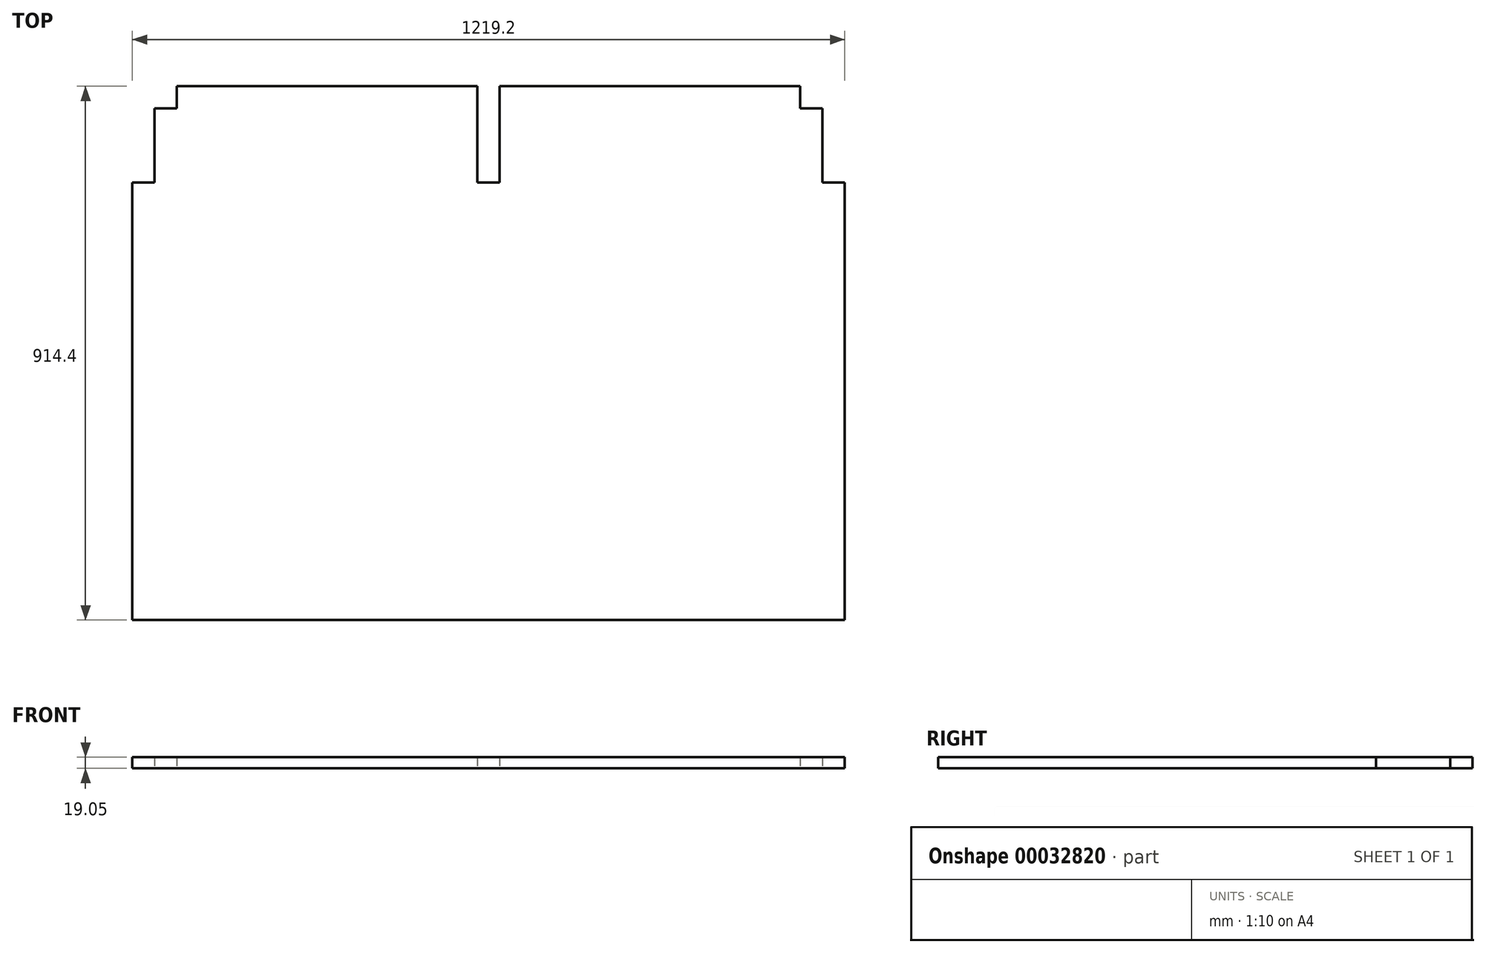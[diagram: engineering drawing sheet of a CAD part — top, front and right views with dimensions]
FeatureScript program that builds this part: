
annotation { "Feature Type Name" : "Feature", "Feature Type Description" : "" }
export const myFeature = defineFeature(function(context is Context, id is Id, definition is map)
    precondition{}
    {
        {
            var Q0;
            Q0=qCreatedBy(makeId("Top.planeOp"),FACE);
            var sketch = newSketch(context, id + "F0", { "sketchPlane" : qUnion([Q0])});
            skLineSegment(sketch, "E0.rect.bottom", {"start": v(-533.4, 539.75) * mm, "end": v(-19.05, 539.75) * mm});
            skLineSegment(sketch, "E0.rect.top", {"start": v(-609.6, -374.65) * mm, "end": v(609.6, -374.65) * mm});
            skLineSegment(sketch, "E0.rect.left", {"start": v(-609.6, 374.65) * mm, "end": v(-609.6, -374.65) * mm});
            skLineSegment(sketch, "E0.rect.right", {"start": v(609.6, 374.65) * mm, "end": v(609.6, -374.65) * mm});
            skPoint(sketch, "E0.rect.middle", {"position": v(0, 0) * mm});
            skLineSegment(sketch, "E1", {"start": v(-609.6, 374.65) * mm, "end": v(-571.5, 374.65) * mm});
            skLineSegment(sketch, "E2", {"start": v(-571.5, 374.65) * mm, "end": v(-571.5, 501.65) * mm});
            skLineSegment(sketch, "E3", {"start": v(-19.05, 539.75) * mm, "end": v(-19.05, 374.65) * mm});
            skLineSegment(sketch, "E4", {"start": v(-19.05, 374.65) * mm, "end": v(19.05, 374.65) * mm});
            skLineSegment(sketch, "E5", {"start": v(19.05, 374.65) * mm, "end": v(19.05, 539.75) * mm});
            skLineSegment(sketch, "E6", {"start": v(571.5, 501.65) * mm, "end": v(571.5, 374.65) * mm});
            skLineSegment(sketch, "E7", {"start": v(571.5, 374.65) * mm, "end": v(609.6, 374.65) * mm});
            skLineSegment(sketch, "E8", {"start": v(0, 374.65) * mm, "end": v(0, 0) * mm, "construction": true});
            skLineSegment(sketch, "E9.trimOffspring", {"start": v(19.05, 539.75) * mm, "end": v(533.4, 539.75) * mm});
            skLineSegment(sketch, "E10", {"start": v(0, -374.65) * mm, "end": v(0, 0) * mm, "construction": true});
            skLineSegment(sketch, "E11", {"start": v(609.6, 0) * mm, "end": v(0, 0) * mm, "construction": true});
            skLineSegment(sketch, "E12", {"start": v(-609.6, 0) * mm, "end": v(0, 0) * mm, "construction": true});
            skLineSegment(sketch, "E13", {"start": v(-571.5, 501.65) * mm, "end": v(-533.4, 501.65) * mm});
            skLineSegment(sketch, "E14", {"start": v(-533.4, 501.65) * mm, "end": v(-533.4, 539.75) * mm});
            skLineSegment(sketch, "E15", {"start": v(533.4, 539.75) * mm, "end": v(533.4, 501.65) * mm});
            skLineSegment(sketch, "E16", {"start": v(533.4, 501.65) * mm, "end": v(571.5, 501.65) * mm});
            skSolve(sketch);
        }
        {
            var Q0;
            Q0=makeQuery(id+"F0.imprint","IMPRINT",FACE,{"disambiguationData":[TD([[makeQuery(id+"F0.imprint","IMPRINT",EDGE,{"derivedFrom":sQuery(id+"F0.wireOp",EDGE,"E0.rect.bottom")}),-1.0]])]});
            extrude(context, id + "F1", {"entities" : qUnion([Q0]), "depth" : 19.05 * mm});
        }
    });
